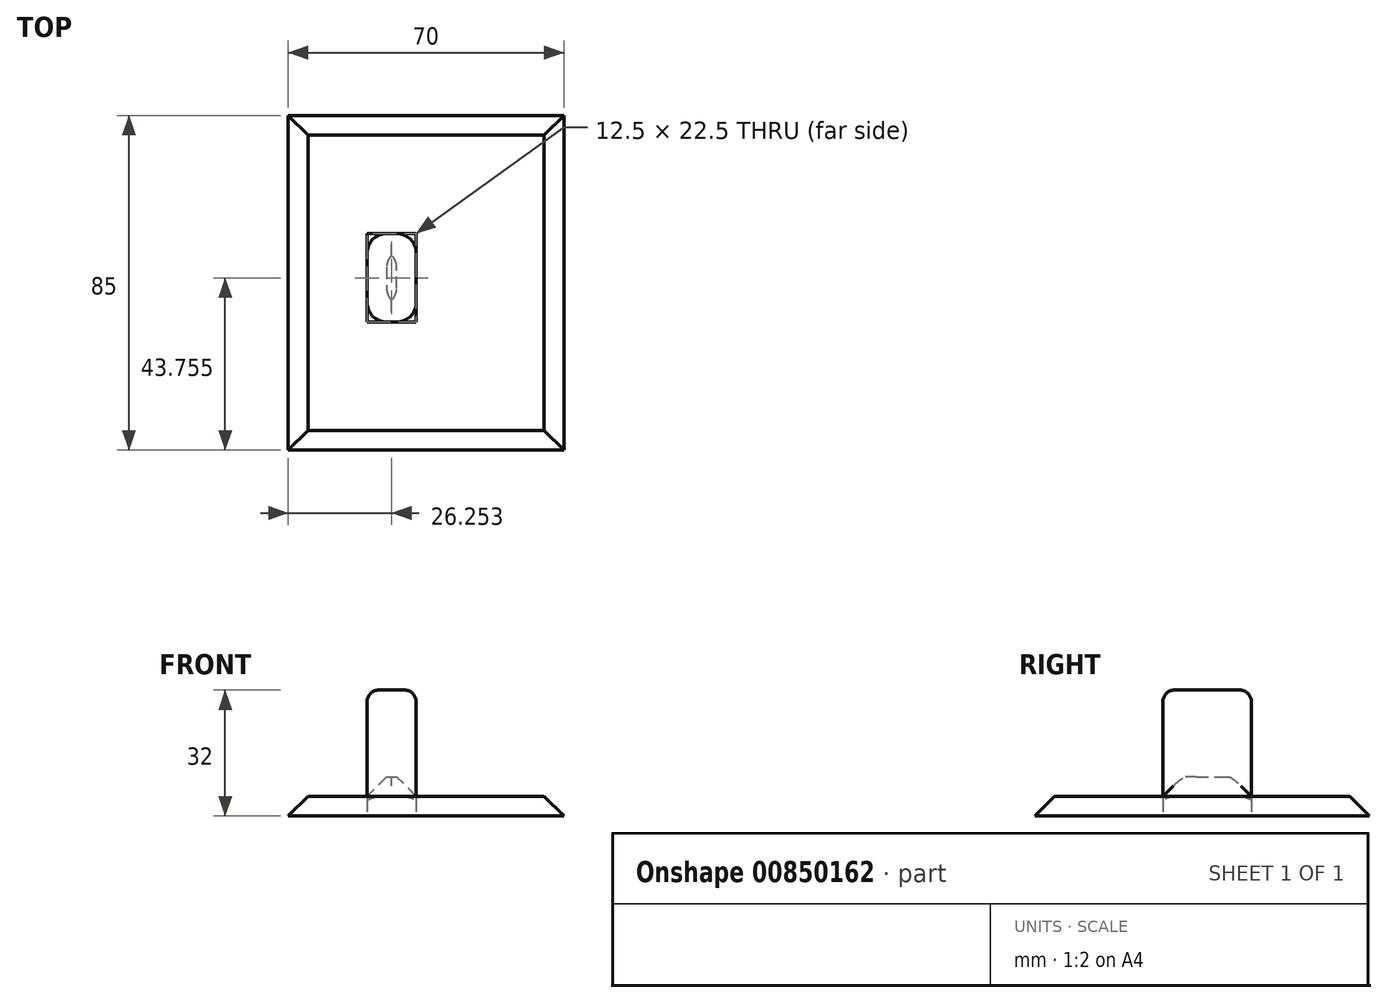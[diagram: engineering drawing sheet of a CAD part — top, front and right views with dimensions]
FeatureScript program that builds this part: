
annotation { "Feature Type Name" : "Feature", "Feature Type Description" : "" }
export const myFeature = defineFeature(function(context is Context, id is Id, definition is map)
    precondition{}
    {
        {
            var Q0;
            Q0=qCreatedBy(makeId("Top.planeOp"),FACE);
            var sketch = newSketch(context, id + "F0", { "sketchPlane" : qUnion([Q0])});
            skLineSegment(sketch, "E0.bottom", {"start": v(-33.7, -17.29) * mm, "end": v(36.3, -17.29) * mm});
            skLineSegment(sketch, "E0.top", {"start": v(-33.7, 67.71) * mm, "end": v(36.3, 67.71) * mm});
            skLineSegment(sketch, "E0.left", {"start": v(-33.7, -17.29) * mm, "end": v(-33.7, 67.71) * mm});
            skLineSegment(sketch, "E0.right", {"start": v(36.3, -17.29) * mm, "end": v(36.3, 67.71) * mm});
            skLineSegment(sketch, "E1.bottom", {"start": v(-13.7, 37.71) * mm, "end": v(-1.2, 37.71) * mm});
            skLineSegment(sketch, "E1.top", {"start": v(-13.7, 15.21) * mm, "end": v(-1.2, 15.21) * mm});
            skLineSegment(sketch, "E1.left", {"start": v(-13.7, 37.71) * mm, "end": v(-13.7, 15.21) * mm});
            skLineSegment(sketch, "E1.right", {"start": v(-1.2, 37.71) * mm, "end": v(-1.2, 15.21) * mm});
            skSolve(sketch);
        }
        {
            var Q0;
            Q0 = qSketchRegion(id + "F0", true);
            extrude(context, id + "F1", {"entities" : qUnion([Q0]), "depth" : 5 * mm, "offsetDistance" : 25 * mm});
        }
        {
            var Q0;
            Q0=makeQuery(id+"F1.opExtrude","CAP_EDGE",EDGE,{"disambiguationData":[OSD([sQuery(id+"F0.wireOp",EDGE,"E0.left")])],"isStart":false});
            var Q1;
            Q1=makeQuery(id+"F1.opExtrude","CAP_EDGE",EDGE,{"disambiguationData":[OSD([sQuery(id+"F0.wireOp",EDGE,"E0.bottom")])],"isStart":false});
            var Q2;
            Q2=makeQuery(id+"F1.opExtrude","CAP_EDGE",EDGE,{"disambiguationData":[OSD([sQuery(id+"F0.wireOp",EDGE,"E0.right")])],"isStart":false});
            var Q3;
            Q3=makeQuery(id+"F1.opExtrude","CAP_EDGE",EDGE,{"disambiguationData":[OSD([sQuery(id+"F0.wireOp",EDGE,"E0.top")])],"isStart":false});
            chamfer(context, id + "F2", {"entities" : qUnion([Q0, Q1, Q2, Q3]), "width" : 5 * mm, "tangentPropagation" : true});
        }
        {
            var Q0;
            Q0=makeQuery(id+"F0.imprint","IMPRINT",FACE,{"disambiguationData":[TD([[makeQuery(id+"F0.imprint","IMPRINT",EDGE,{"derivedFrom":sQuery(id+"F0.wireOp",EDGE,"E1.bottom")}),-1.0]])]});
            extrude(context, id + "F3", {"entities" : qUnion([Q0]), "depth" : 32 * mm, "offsetDistance" : 25 * mm});
        }
        {
            var Q0;
            Q0=makeQuery(id+"F3.opExtrude","CAP_EDGE",EDGE,{"disambiguationData":[OSD([sQuery(id+"F0.wireOp",EDGE,"E1.left")])],"isStart":false});
            var Q1;
            Q1=makeQuery(id+"F3.opExtrude","CAP_EDGE",EDGE,{"disambiguationData":[OSD([sQuery(id+"F0.wireOp",EDGE,"E1.top")])],"isStart":false});
            var Q2;
            Q2=makeQuery(id+"F3.opExtrude","CAP_EDGE",EDGE,{"disambiguationData":[OSD([sQuery(id+"F0.wireOp",EDGE,"E1.bottom")])],"isStart":false});
            var Q3;
            Q3=makeQuery(id+"F3.opExtrude","CAP_EDGE",EDGE,{"disambiguationData":[OSD([sQuery(id+"F0.wireOp",EDGE,"E1.right")])],"isStart":false});
            var Q4;
            Q4=makeQuery(id+"F3.opExtrude","CAP_FACE",FACE,{"disambiguationData":[OSD([sQuery(id+"F0.wireOp",EDGE,"E1.bottom"),sQuery(id+"F0.wireOp",EDGE,"E1.top"),sQuery(id+"F0.wireOp",EDGE,"E1.left"),sQuery(id+"F0.wireOp",EDGE,"E1.right")])],"isStart":false});
            fillet(context, id + "F4", {"entities" : qUnion([Q0, Q1, Q2, Q3, Q4]), "radius" : 3 * mm, "allowEdgeOverflow" : false});
        }
        {
            var Q0;
            Q0=makeQuery(id+"F3.opExtrude","SWEPT_EDGE",EDGE,{"disambiguationData":[OSD([sQuery(id+"F0.wireOp",EDGE,"E1.bottom"),sQuery(id+"F0.wireOp",EDGE,"E1.right")])]});
            var Q1;
            Q1=makeQuery(id+"F3.opExtrude","SWEPT_EDGE",EDGE,{"disambiguationData":[OSD([sQuery(id+"F0.wireOp",EDGE,"E1.top"),sQuery(id+"F0.wireOp",EDGE,"E1.right")])]});
            var Q2;
            Q2=makeQuery(id+"F3.opExtrude","SWEPT_EDGE",EDGE,{"disambiguationData":[OSD([sQuery(id+"F0.wireOp",EDGE,"E1.top"),sQuery(id+"F0.wireOp",EDGE,"E1.left")])]});
            var Q3;
            Q3=makeQuery(id+"F3.opExtrude","SWEPT_EDGE",EDGE,{"disambiguationData":[OSD([sQuery(id+"F0.wireOp",EDGE,"E1.bottom"),sQuery(id+"F0.wireOp",EDGE,"E1.left")])]});
            var Q4;
            Q4=makeQuery(id+"F4.opFillet","BLEND_FACE",FACE,{"disambiguationData":[OSD([sQuery(id+"F0.wireOp",EDGE,"E1.left")])]});
            fillet(context, id + "F5", {"entities" : qUnion([Q0, Q1, Q2, Q3, Q4]), "radius" : 5 * mm, "tangentPropagation" : true, "allowEdgeOverflow" : false});
        }
        {
            var Q0;
            Q0=makeQuery(id+"F0.imprint","IMPRINT",FACE,{"disambiguationData":[TD([[makeQuery(id+"F0.imprint","IMPRINT",EDGE,{"derivedFrom":sQuery(id+"F0.wireOp",EDGE,"E1.bottom")}),-1.0]])]});
            extrude(context, id + "F6", {"entities" : qUnion([Q0]), "depth" : 10 * mm, "offsetDistance" : 25 * mm});
        }
        {
            var Q0;
            Q0=makeQuery(id+"F6.opExtrude","CAP_EDGE",EDGE,{"disambiguationData":[OSD([sQuery(id+"F0.wireOp",EDGE,"E1.left")])],"isStart":false});
            var Q1;
            Q1=makeQuery(id+"F6.opExtrude","CAP_EDGE",EDGE,{"disambiguationData":[OSD([sQuery(id+"F0.wireOp",EDGE,"E1.top")])],"isStart":false});
            var Q2;
            Q2=makeQuery(id+"F6.opExtrude","CAP_EDGE",EDGE,{"disambiguationData":[OSD([sQuery(id+"F0.wireOp",EDGE,"E1.right")])],"isStart":false});
            var Q3;
            Q3=makeQuery(id+"F6.opExtrude","CAP_EDGE",EDGE,{"disambiguationData":[OSD([sQuery(id+"F0.wireOp",EDGE,"E1.bottom")])],"isStart":false});
            chamfer(context, id + "F7", {"entities" : qUnion([Q0, Q1, Q2, Q3]), "width" : 5 * mm, "tangentPropagation" : true});
        }
        {
            var Q0;
            Q0=makeQuery(id+"F7.opChamfer","BLEND_EDGE",EDGE,{"blendedFrom":[makeQuery(id+"F6.opExtrude","CAP_EDGE",EDGE,{"disambiguationData":[OSD([sQuery(id+"F0.wireOp",EDGE,"E1.bottom")])],"isStart":false}),makeQuery(id+"F6.opExtrude","CAP_EDGE",EDGE,{"disambiguationData":[OSD([sQuery(id+"F0.wireOp",EDGE,"E1.left")])],"isStart":false})],"blendedInto":[]});
            var Q1;
            Q1=makeQuery(id+"F7.opChamfer","BLEND_EDGE",EDGE,{"blendedFrom":[makeQuery(id+"F6.opExtrude","CAP_EDGE",EDGE,{"disambiguationData":[OSD([sQuery(id+"F0.wireOp",EDGE,"E1.bottom")])],"isStart":false}),makeQuery(id+"F6.opExtrude","CAP_EDGE",EDGE,{"disambiguationData":[OSD([sQuery(id+"F0.wireOp",EDGE,"E1.right")])],"isStart":false})],"blendedInto":[]});
            var Q2;
            Q2=makeQuery(id+"F7.opChamfer","BLEND_EDGE",EDGE,{"blendedFrom":[makeQuery(id+"F6.opExtrude","CAP_EDGE",EDGE,{"disambiguationData":[OSD([sQuery(id+"F0.wireOp",EDGE,"E1.top")])],"isStart":false}),makeQuery(id+"F6.opExtrude","CAP_EDGE",EDGE,{"disambiguationData":[OSD([sQuery(id+"F0.wireOp",EDGE,"E1.left")])],"isStart":false})],"blendedInto":[]});
            var Q3;
            Q3=makeQuery(id+"F7.opChamfer","BLEND_EDGE",EDGE,{"blendedFrom":[makeQuery(id+"F6.opExtrude","CAP_EDGE",EDGE,{"disambiguationData":[OSD([sQuery(id+"F0.wireOp",EDGE,"E1.top")])],"isStart":false}),makeQuery(id+"F6.opExtrude","CAP_EDGE",EDGE,{"disambiguationData":[OSD([sQuery(id+"F0.wireOp",EDGE,"E1.right")])],"isStart":false})],"blendedInto":[]});
            fillet(context, id + "F8", {"entities" : qUnion([Q0, Q1, Q2, Q3]), "radius" : 5 * mm, "tangentPropagation" : true, "allowEdgeOverflow" : false});
        }
    });
